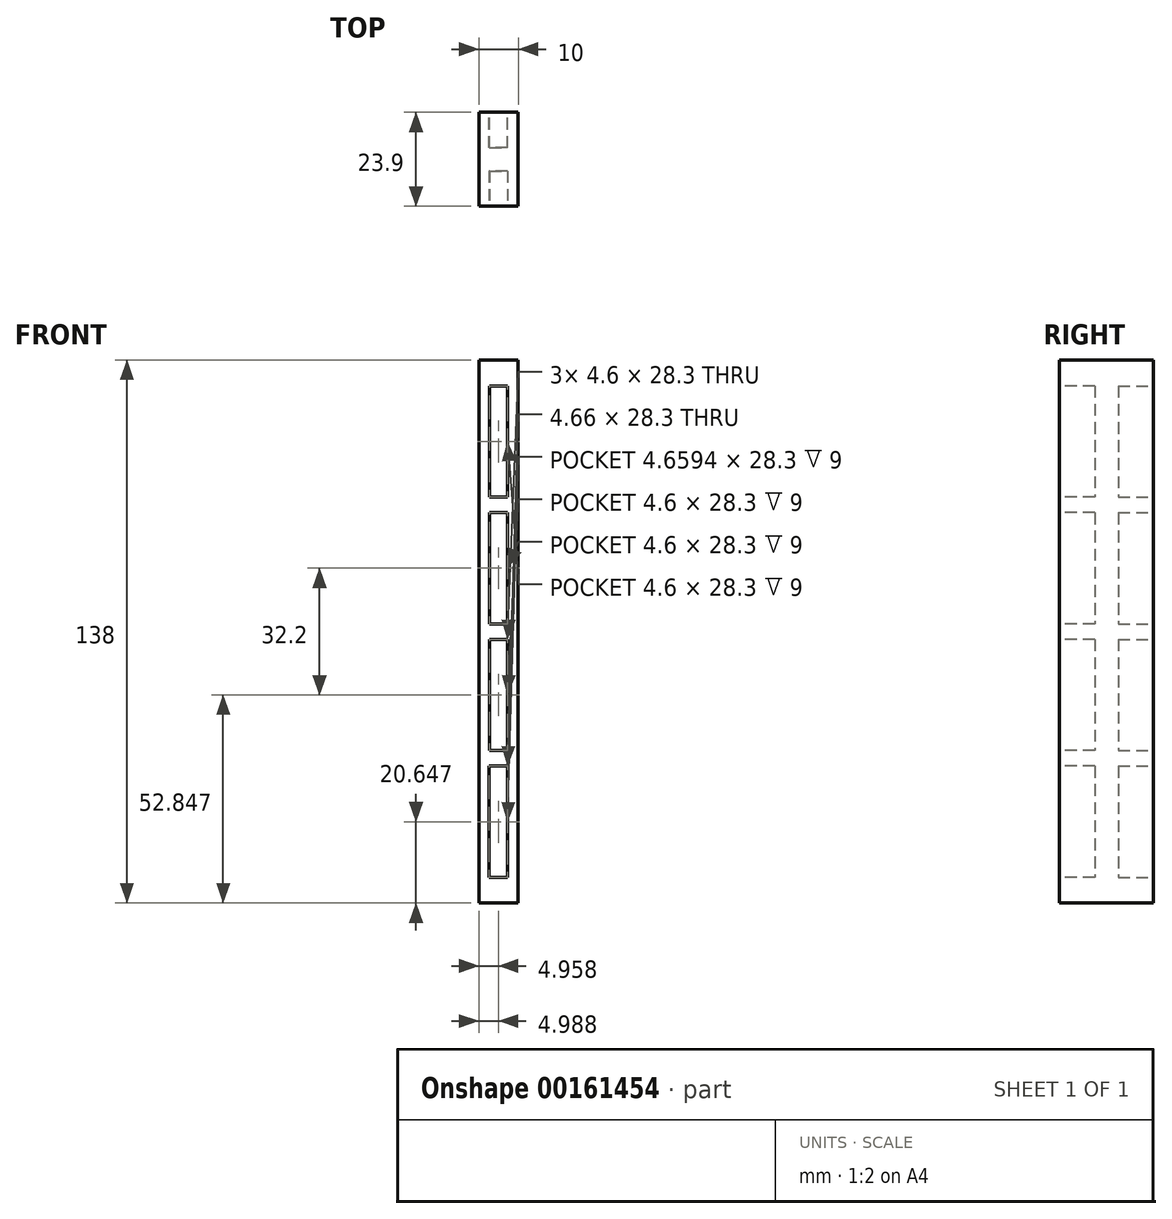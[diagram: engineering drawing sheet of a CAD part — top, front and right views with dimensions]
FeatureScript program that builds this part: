
annotation { "Feature Type Name" : "Feature", "Feature Type Description" : "" }
export const myFeature = defineFeature(function(context is Context, id is Id, definition is map)
    precondition{}
    {
        {
            var Q0;
            Q0=qCreatedBy(makeId("Front.planeOp"),FACE);
            var sketch = newSketch(context, id + "F0", { "sketchPlane" : qUnion([Q0])});
            skLineSegment(sketch, "E0.bottom", {"start": v(-30.25, 56.68) * mm, "end": v(-20.25, 56.68) * mm});
            skLineSegment(sketch, "E0.top", {"start": v(-30.25, -81.32) * mm, "end": v(-20.25, -81.32) * mm});
            skLineSegment(sketch, "E0.left", {"start": v(-30.25, 56.68) * mm, "end": v(-30.25, -81.32) * mm});
            skLineSegment(sketch, "E0.right", {"start": v(-20.25, 56.68) * mm, "end": v(-20.25, -81.32) * mm});
            skLineSegment(sketch, "E1.bottom", {"start": v(-27.56, 50.08) * mm, "end": v(-22.96, 50.08) * mm});
            skLineSegment(sketch, "E1.top", {"start": v(-27.56, 21.78) * mm, "end": v(-22.96, 21.78) * mm});
            skLineSegment(sketch, "E1.left", {"start": v(-27.56, 50.08) * mm, "end": v(-27.56, 21.78) * mm});
            skLineSegment(sketch, "E1.right", {"start": v(-22.96, 50.08) * mm, "end": v(-22.96, 21.78) * mm});
            skLineSegment(sketch, "E2", {"start": v(-26.53, 56.68) * mm, "end": v(-26.53, 50.08) * mm, "construction": true});
            skLineSegment(sketch, "E3", {"start": v(-27.56, 45.9) * mm, "end": v(-30.25, 45.9) * mm, "construction": true});
            skLineSegment(sketch, "E4", {"start": v(-22.96, 46.31) * mm, "end": v(-20.25, 46.31) * mm, "construction": true});
            skLineSegment(sketch, "E5", {"start": v(-25.26, 21.78) * mm, "end": v(-25.26, 17.88) * mm, "construction": true});
            skLineSegment(sketch, "E6", {"start": v(-27.56, 21.78) * mm, "end": v(-27.56, 17.88) * mm, "construction": true});
            skLineSegment(sketch, "E7", {"start": v(-22.96, 21.78) * mm, "end": v(-22.96, 17.88) * mm, "construction": true});
            skLineSegment(sketch, "E8.bottom", {"start": v(-27.56, 17.88) * mm, "end": v(-22.96, 17.88) * mm});
            skLineSegment(sketch, "E8.top", {"start": v(-27.56, -10.42) * mm, "end": v(-22.96, -10.42) * mm});
            skLineSegment(sketch, "E8.left", {"start": v(-27.56, 17.88) * mm, "end": v(-27.56, -10.42) * mm});
            skLineSegment(sketch, "E8.right", {"start": v(-22.96, 17.88) * mm, "end": v(-22.96, -10.42) * mm});
            skLineSegment(sketch, "E9", {"start": v(-22.96, -10.42) * mm, "end": v(-22.96, -14.32) * mm, "construction": true});
            skLineSegment(sketch, "E10", {"start": v(-27.56, -10.42) * mm, "end": v(-27.56, -14.32) * mm, "construction": true});
            skLineSegment(sketch, "E11.bottom", {"start": v(-27.56, -14.32) * mm, "end": v(-22.96, -14.32) * mm});
            skLineSegment(sketch, "E11.top", {"start": v(-27.56, -42.62) * mm, "end": v(-22.96, -42.62) * mm});
            skLineSegment(sketch, "E11.left", {"start": v(-27.56, -14.32) * mm, "end": v(-27.56, -42.62) * mm});
            skLineSegment(sketch, "E11.right", {"start": v(-22.96, -14.32) * mm, "end": v(-22.96, -42.62) * mm});
            skLineSegment(sketch, "E12", {"start": v(-27.56, -41.18) * mm, "end": v(-27.56, -42.62) * mm});
            skLineSegment(sketch, "E13", {"start": v(-22.96, -42.62) * mm, "end": v(-22.96, -46.52) * mm, "construction": true});
            skLineSegment(sketch, "E14.bottom", {"start": v(-22.96, -46.52) * mm, "end": v(-27.62, -46.52) * mm});
            skLineSegment(sketch, "E14.top", {"start": v(-22.96, -74.82) * mm, "end": v(-27.62, -74.82) * mm});
            skLineSegment(sketch, "E14.left", {"start": v(-22.96, -46.52) * mm, "end": v(-22.96, -74.82) * mm});
            skLineSegment(sketch, "E14.right", {"start": v(-27.62, -46.52) * mm, "end": v(-27.62, -74.82) * mm});
            skLineSegment(sketch, "E15", {"start": v(-22.96, -74.82) * mm, "end": v(-22.96, -81.32) * mm, "construction": true});
            skSolve(sketch);
        }
        {
            var Q0;
            Q0=makeQuery(id+"F0.imprint","IMPRINT",FACE,{"disambiguationData":[TD([[makeQuery(id+"F0.imprint","IMPRINT",EDGE,{"derivedFrom":sQuery(id+"F0.wireOp",EDGE,"E0.bottom")}),-1.0]])]});
            var Q1;
            Q1=makeQuery(id+"F0.imprint","IMPRINT",FACE,{"disambiguationData":[TD([[makeQuery(id+"F0.imprint","IMPRINT",EDGE,{"derivedFrom":sQuery(id+"F0.wireOp",EDGE,"E1.bottom")}),-1.0]])]});
            var Q2;
            Q2=makeQuery(id+"F0.imprint","IMPRINT",FACE,{"disambiguationData":[TD([[makeQuery(id+"F0.imprint","IMPRINT",EDGE,{"derivedFrom":sQuery(id+"F0.wireOp",EDGE,"E8.bottom")}),-1.0]])]});
            var Q3;
            Q3=makeQuery(id+"F0.imprint","IMPRINT",FACE,{"disambiguationData":[TD([[makeQuery(id+"F0.imprint","IMPRINT",EDGE,{"derivedFrom":sQuery(id+"F0.wireOp",EDGE,"E11.bottom")}),-1.0]])]});
            var Q4;
            Q4=makeQuery(id+"F0.imprint","IMPRINT",FACE,{"disambiguationData":[TD([[makeQuery(id+"F0.imprint","IMPRINT",EDGE,{"derivedFrom":sQuery(id+"F0.wireOp",EDGE,"E14.bottom")}),1.0]])]});
            extrude(context, id + "F1", {"entities" : qUnion([Q0, Q1, Q2, Q3, Q4]), "depth" : 11.95 * mm});
        }
        {
            var Q0;
            Q0=makeQuery(id+"F0.imprint","IMPRINT",FACE,{"disambiguationData":[TD([[makeQuery(id+"F0.imprint","IMPRINT",EDGE,{"derivedFrom":sQuery(id+"F0.wireOp",EDGE,"E1.bottom")}),-1.0]])]});
            var Q1;
            Q1=makeQuery(id+"F0.imprint","IMPRINT",FACE,{"disambiguationData":[TD([[makeQuery(id+"F0.imprint","IMPRINT",EDGE,{"derivedFrom":sQuery(id+"F0.wireOp",EDGE,"E8.bottom")}),-1.0]])]});
            var Q2;
            Q2=makeQuery(id+"F0.imprint","IMPRINT",FACE,{"disambiguationData":[TD([[makeQuery(id+"F0.imprint","IMPRINT",EDGE,{"derivedFrom":sQuery(id+"F0.wireOp",EDGE,"E11.bottom")}),-1.0]])]});
            var Q3;
            Q3=makeQuery(id+"F0.imprint","IMPRINT",FACE,{"disambiguationData":[TD([[makeQuery(id+"F0.imprint","IMPRINT",EDGE,{"derivedFrom":sQuery(id+"F0.wireOp",EDGE,"E14.bottom")}),1.0]])]});
            extrude(context, id + "F2", {"entities" : qUnion([Q0, Q1, Q2, Q3]), "operationType" : NewBodyOperationType.REMOVE, "depth" : 9 * mm});
        }
        {
            var Q0;
            Q0=makeQuery(id+"F1.opExtrude","SWEPT_BODY",BODY,{"disambiguationData":[OSD([sQuery(id+"F0.wireOp",EDGE,"E0.bottom"),sQuery(id+"F0.wireOp",EDGE,"E0.top"),sQuery(id+"F0.wireOp",EDGE,"E0.left"),sQuery(id+"F0.wireOp",EDGE,"E0.right")])]});
            var Q1;
            Q1=makeQuery(id+"F1.opExtrude","CAP_FACE",FACE,{"disambiguationData":[OSD([sQuery(id+"F0.wireOp",EDGE,"E0.bottom"),sQuery(id+"F0.wireOp",EDGE,"E0.top"),sQuery(id+"F0.wireOp",EDGE,"E0.left"),sQuery(id+"F0.wireOp",EDGE,"E0.right")])],"isStart":false});
            mirror(context, id + "F3", {"operationType" : NewBodyOperationType.ADD, "entities" : qUnion([Q0]), "mirrorPlane" : qUnion([Q1])});
        }
    });
